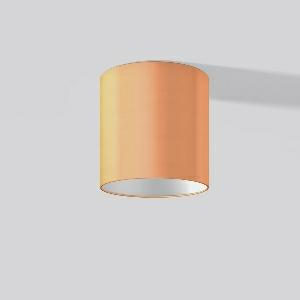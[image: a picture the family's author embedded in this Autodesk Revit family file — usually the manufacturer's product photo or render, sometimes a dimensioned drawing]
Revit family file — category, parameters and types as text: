
# Revit family: toledo_flatliner_901630_002_112d
name_source: partatom
category: Lighting Fixtures
units: mm (PartAtom-declared; Revit-internal decimal feet)

## family parameters
Cut with Voids When Loaded = No
Host = Face
Light Source = No
Part Type = Normal
Room Calculation Point = No
Round Connector Dimension = Use Diameter
Shared = No

## types (1)
- 982300.002 (1 x LED Modul 830, 610 lm, 3000)
    Apparent Load = 8 VA
    CIE Flux Codes = 56 78 92 81 100
    Color Rendering = 80
    Color Temperature = 3000
    Default Elevation = 1800 mm
    Description = Series: TOLEDO FLATLINER
Decorative ceiling luminaire for interior decoration. Base luminaire prepared for the installation of fabric lampshade. Cylinder housing sheet steel, powder-coated. Housing: die cast aluminium and sheet steel, powder-coated. Bezel ring: die-cast aluminium, powder-coated. Lightguide and diffuser made of non-yellowing plastic (PMMA) opal matt. Modular design: With the basic luminaire, a square or cylindrical fabric lampshade must always be ordered separately. Fabric lampshades can be fitted to the basic luminaire without tools. Order satin finish diffuser as separate accessory. 
Colour: white
Diameter: 202 mm
Height: 65 mm
Lamp: LED
Socket: without socket
Colour temperature: 3000K
Colour rendering index (CRI): 80
System power: 7.7 W
Rated luminous flux: 610 lm
Luminous efficiency: 79 lm/W
Control gear: Regulated power supply
Protection class: II
Type of protection: IP 40
    Height = 65 mm
    Lamp = 1 x LED Modul 830
    Lamp Light Flux = 610 lm
    Lamp count = 1
    Length = 202 mm
    Lifetime = 50000 h
    Luminous efficacy = 79 lm/W
    Manufacturer = RZB
    ModVariant = No
    Model = 901630.002
    Mounting Place = Ceiling
    Mounting Type = Surface mounted
    Number of Poles = 1
    OnlyDefault = Yes
    Power Factor = 1
    Product Name = TOLEDO FLATLINER
    Product group = Surface mounted ceiling Fabric lampshade luminaires
    ProductGroupID = 313
    Protection Class = Protection class II
    Protection Degree = IP 40
    RLX_Detail_Level = 1
    RLX_Emergency_Light_Flux = 0 lm
    RLX_Emergency_Type = 0
    RLX_Emergency_Type_DB = No
    RlxData = <blob elided: 62693 chars, md5=fd21def6>
    Socket = socket
    Standby Power = 0 W
    System Light Flux = 610 lm
    System Power = 8 W
    Type Image = toledo_flatliner_anbau_rund_orange_odeckel.jpg
    URL = http://relux.com
    VarID = 982300_002_5a54
    Voltage = 230 V
    Voltage Range = 220-240 V
    Weight = 0.00 kg
    Width = 0 mm  [stored 0 ft]

note: [stored X ft] marks values corroborated as IEEE doubles in the binary element streams (Revit-internal decimal feet)

## geometry (parser evidence)
native form markers: Blend x4, Sweep x12
no freeform markers — native parametric forms only
